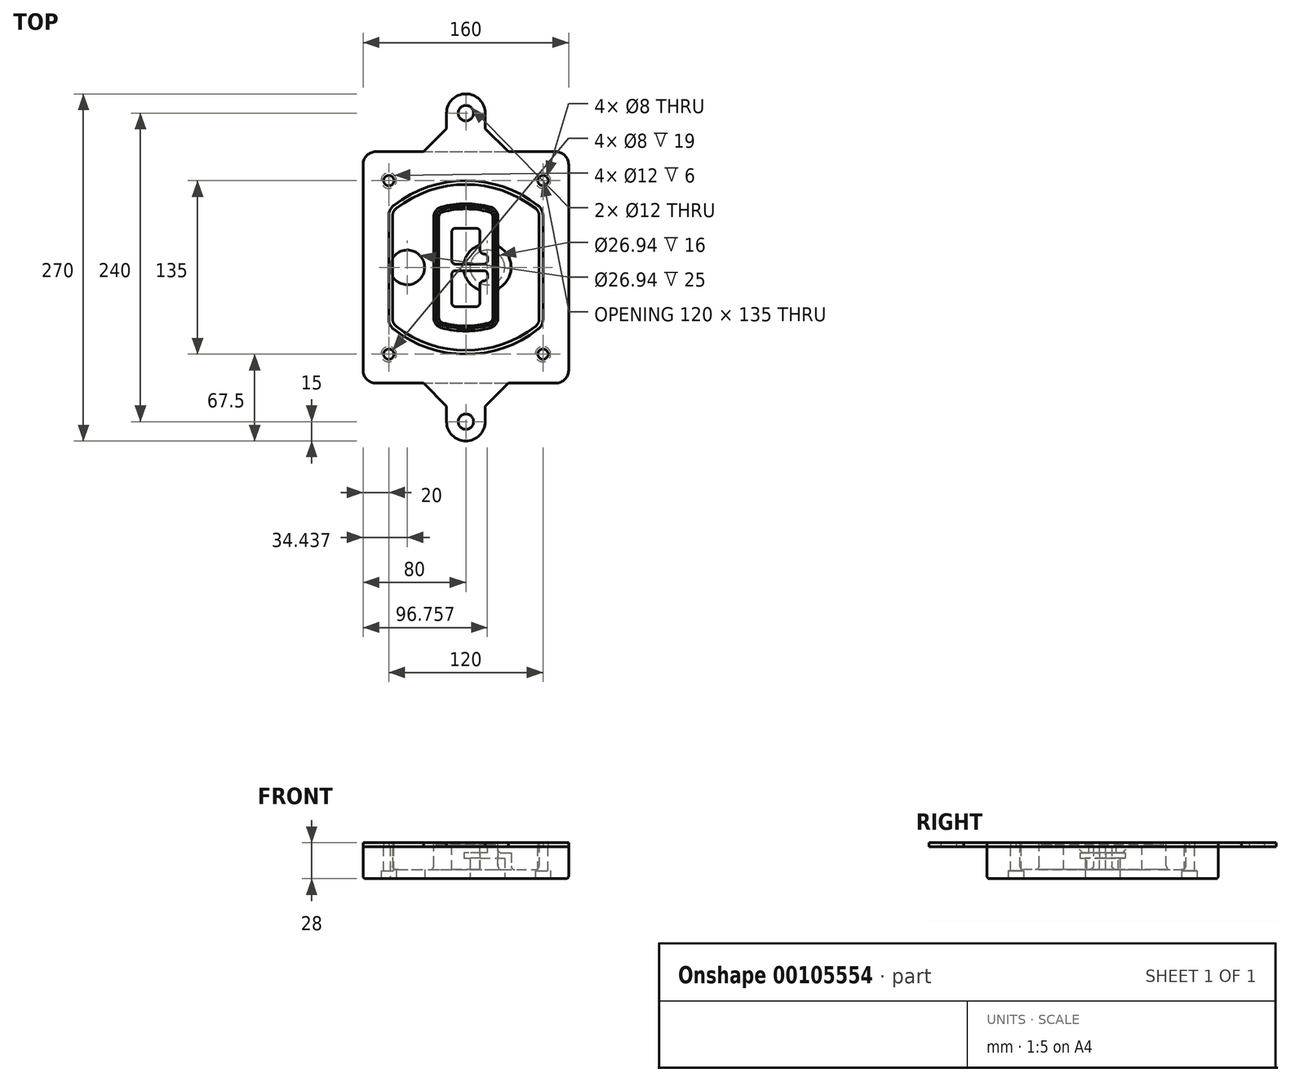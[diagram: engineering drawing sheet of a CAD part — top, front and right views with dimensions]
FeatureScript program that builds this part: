
annotation { "Feature Type Name" : "Feature", "Feature Type Description" : "" }
export const myFeature = defineFeature(function(context is Context, id is Id, definition is map)
    precondition{}
    {
        {
            var Q0;
            Q0=qCreatedBy(makeId("Top.planeOp"),FACE);
            var sketch = newSketch(context, id + "F0", { "sketchPlane" : qUnion([Q0])});
            skPoint(sketch, "E0.rect.middle", {"position": v(0, 0) * mm});
            skLineSegment(sketch, "E1.bottom", {"start": v(-70, -90) * mm, "end": v(70, -90) * mm});
            skLineSegment(sketch, "E1.top", {"start": v(-70, 90) * mm, "end": v(70, 90) * mm});
            skLineSegment(sketch, "E1.left", {"start": v(-80, -80) * mm, "end": v(-80, 80) * mm});
            skLineSegment(sketch, "E1.right", {"start": v(80, -80) * mm, "end": v(80, 80) * mm});
            skLineSegment(sketch, "E2", {"start": v(-80, 90) * mm, "end": v(80, -90) * mm, "construction": true});
            skLineSegment(sketch, "E3", {"start": v(80, 90) * mm, "end": v(-80, -90) * mm, "construction": true});
            skCircle(sketch, "E4", {"center": v(-60, 67.5) * mm, "radius": 4 * mm});
            skCircle(sketch, "E5", {"center": v(60, 67.5) * mm, "radius": 4 * mm});
            skCircle(sketch, "E6", {"center": v(60, -67.5) * mm, "radius": 4 * mm});
            skCircle(sketch, "E7", {"center": v(-60, -67.5) * mm, "radius": 4 * mm});
            skLineSegment(sketch, "E8", {"start": v(-60, 67.5) * mm, "end": v(60, 67.5) * mm, "construction": true});
            skLineSegment(sketch, "E9", {"start": v(60, 67.5) * mm, "end": v(60, -67.5) * mm, "construction": true});
            skLineSegment(sketch, "E10", {"start": v(60, -67.5) * mm, "end": v(-60, -67.5) * mm, "construction": true});
            skLineSegment(sketch, "E11", {"start": v(-60, -67.5) * mm, "end": v(-60, 67.5) * mm, "construction": true});
            skLineSegment(sketch, "E12", {"start": v(-60, 40.3) * mm, "end": v(-60, -40.3) * mm});
            skLineSegment(sketch, "E13", {"start": v(60, 40.3) * mm, "end": v(60, -40.3) * mm});
            skArc(sketch, "E14", {"start": v(56.15, 48.18) * mm, "mid": v(0, 67.5) * mm, "end": v(-56.15, 48.18) * mm});
            skArc(sketch, "E15", {"start": v(-56.15, -48.18) * mm, "mid": v(0, -67.5) * mm, "end": v(56.15, -48.18) * mm});
            skLineSegment(sketch, "E16", {"start": v(-60, 0) * mm, "end": v(60, 0) * mm, "construction": true});
            skPoint(sketch, "E17.visualSharp", {"position": v(-60, -45) * mm});
            skArc(sketch, "E17.filletArc", {"start": v(-60, -40.3) * mm, "mid": v(-58.99, -44.68) * mm, "end": v(-56.15, -48.18) * mm});
            skPoint(sketch, "E18.visualSharp", {"position": v(-60, 45) * mm});
            skArc(sketch, "E18.filletArc", {"start": v(-56.15, 48.18) * mm, "mid": v(-58.99, 44.68) * mm, "end": v(-60, 40.3) * mm});
            skPoint(sketch, "E19.visualSharp", {"position": v(60, 45) * mm});
            skArc(sketch, "E19.filletArc", {"start": v(60, 40.3) * mm, "mid": v(58.99, 44.68) * mm, "end": v(56.15, 48.18) * mm});
            skPoint(sketch, "E20.visualSharp", {"position": v(60, -45) * mm});
            skArc(sketch, "E20.filletArc", {"start": v(56.15, -48.18) * mm, "mid": v(58.99, -44.68) * mm, "end": v(60, -40.3) * mm});
            skPoint(sketch, "E21.visualSharp", {"position": v(-80, 90) * mm});
            skArc(sketch, "E21.filletArc", {"start": v(-70, 90) * mm, "mid": v(-77.07, 87.07) * mm, "end": v(-80, 80) * mm});
            skPoint(sketch, "E22.visualSharp", {"position": v(80, 90) * mm});
            skArc(sketch, "E22.filletArc", {"start": v(80, 80) * mm, "mid": v(77.07, 87.07) * mm, "end": v(70, 90) * mm});
            skPoint(sketch, "E23.visualSharp", {"position": v(80, -90) * mm});
            skArc(sketch, "E23.filletArc", {"start": v(70, -90) * mm, "mid": v(77.07, -87.07) * mm, "end": v(80, -80) * mm});
            skPoint(sketch, "E24.visualSharp", {"position": v(-80, -90) * mm});
            skArc(sketch, "E24.filletArc", {"start": v(-80, -80) * mm, "mid": v(-77.07, -87.07) * mm, "end": v(-70, -90) * mm});
            skArc(sketch, "E25.0", {"start": v(57, 40.3) * mm, "mid": v(56.3, 43.36) * mm, "end": v(54.3, 45.81) * mm});
            skLineSegment(sketch, "E25.1", {"start": v(57, 40.3) * mm, "end": v(57, -40.3) * mm});
            skArc(sketch, "E25.2", {"start": v(54.3, -45.81) * mm, "mid": v(56.3, -43.36) * mm, "end": v(57, -40.3) * mm});
            skArc(sketch, "E25.3", {"start": v(-54.3, -45.81) * mm, "mid": v(0, -64.5) * mm, "end": v(54.3, -45.81) * mm});
            skArc(sketch, "E25.4", {"start": v(-57, -40.3) * mm, "mid": v(-56.3, -43.36) * mm, "end": v(-54.3, -45.81) * mm});
            skArc(sketch, "E25.5", {"start": v(54.3, 45.81) * mm, "mid": v(0, 64.5) * mm, "end": v(-54.3, 45.81) * mm});
            skLineSegment(sketch, "E25.6", {"start": v(-57, 40.3) * mm, "end": v(-57, -40.3) * mm});
            skArc(sketch, "E25.7", {"start": v(-54.3, 45.81) * mm, "mid": v(-56.3, 43.36) * mm, "end": v(-57, 40.3) * mm});
            skArc(sketch, "E26.0", {"start": v(-58.62, 51.33) * mm, "mid": v(-62.58, 46.43) * mm, "end": v(-64, 40.3) * mm});
            skArc(sketch, "E26.1", {"start": v(58.62, 51.33) * mm, "mid": v(0, 71.5) * mm, "end": v(-58.62, 51.33) * mm});
            skArc(sketch, "E26.2", {"start": v(64, 40.3) * mm, "mid": v(62.58, 46.43) * mm, "end": v(58.62, 51.33) * mm});
            skLineSegment(sketch, "E26.3", {"start": v(64, 40.3) * mm, "end": v(64, -40.3) * mm});
            skArc(sketch, "E26.4", {"start": v(58.62, -51.33) * mm, "mid": v(62.58, -46.43) * mm, "end": v(64, -40.3) * mm});
            skLineSegment(sketch, "E26.5", {"start": v(-64, 40.3) * mm, "end": v(-64, -40.3) * mm});
            skArc(sketch, "E26.6", {"start": v(-58.62, -51.33) * mm, "mid": v(0, -71.5) * mm, "end": v(58.62, -51.33) * mm});
            skArc(sketch, "E26.7", {"start": v(-64, -40.3) * mm, "mid": v(-62.58, -46.43) * mm, "end": v(-58.62, -51.33) * mm});
            skSolve(sketch);
        }
        {
            var Q0;
            Q0=makeQuery(id+"F0.imprint","IMPRINT",FACE,{"disambiguationData":[TD([[makeQuery(id+"F0.imprint","IMPRINT",EDGE,{"derivedFrom":sQuery(id+"F0.wireOp",EDGE,"E1.bottom")}),1.0]])]});
            var Q1;
            Q1=makeQuery(id+"F0.imprint","IMPRINT",FACE,{"disambiguationData":[TD([[makeQuery(id+"F0.imprint","IMPRINT",EDGE,{"derivedFrom":sQuery(id+"F0.wireOp",EDGE,"E12")}),1.0]])]});
            var Q2;
            Q2=makeQuery(id+"F0.imprint","IMPRINT",FACE,{"disambiguationData":[TD([[makeQuery(id+"F0.imprint","IMPRINT",EDGE,{"derivedFrom":sQuery(id+"F0.wireOp",EDGE,"E25.0")}),1.0]])]});
            var Q3;
            Q3=makeQuery(id+"F0.imprint","IMPRINT",FACE,{"disambiguationData":[TD([[makeQuery(id+"F0.imprint","IMPRINT",EDGE,{"derivedFrom":sQuery(id+"F0.wireOp",EDGE,"E12")}),-1.0]])]});
            extrude(context, id + "F1", {"entities" : qUnion([Q0, Q1, Q2, Q3]), "oppositeDirection" : true, "depth" : 25 * mm});
        }
        {
            var Q0;
            Q0=makeQuery(id+"F0.imprint","IMPRINT",FACE,{"disambiguationData":[TD([[makeQuery(id+"F0.imprint","IMPRINT",EDGE,{"derivedFrom":sQuery(id+"F0.wireOp",EDGE,"E12")}),1.0]])]});
            extrude(context, id + "F2", {"entities" : qUnion([Q0]), "operationType" : NewBodyOperationType.ADD, "depth" : 3 * mm});
        }
        {
            var Q0;
            Q0=makeQuery(id+"F0.imprint","IMPRINT",FACE,{"disambiguationData":[TD([[makeQuery(id+"F0.imprint","IMPRINT",EDGE,{"derivedFrom":sQuery(id+"F0.wireOp",EDGE,"E25.0")}),1.0]])]});
            extrude(context, id + "F3", {"entities" : qUnion([Q0]), "operationType" : NewBodyOperationType.REMOVE, "oppositeDirection" : true, "depth" : 18 * mm});
        }
        {
            var Q0;
            Q0=makeQuery(id+"F2.opExtrude","CAP_FACE",FACE,{"disambiguationData":[OSD([sQuery(id+"F0.wireOp",EDGE,"E12"),sQuery(id+"F0.wireOp",EDGE,"E13"),sQuery(id+"F0.wireOp",EDGE,"E14"),sQuery(id+"F0.wireOp",EDGE,"E15"),sQuery(id+"F0.wireOp",EDGE,"E17.filletArc"),sQuery(id+"F0.wireOp",EDGE,"E18.filletArc"),sQuery(id+"F0.wireOp",EDGE,"E19.filletArc"),sQuery(id+"F0.wireOp",EDGE,"E20.filletArc"),sQuery(id+"F0.wireOp",EDGE,"E25.0"),sQuery(id+"F0.wireOp",EDGE,"E25.1"),sQuery(id+"F0.wireOp",EDGE,"E25.2"),sQuery(id+"F0.wireOp",EDGE,"E25.3"),sQuery(id+"F0.wireOp",EDGE,"E25.4"),sQuery(id+"F0.wireOp",EDGE,"E25.5"),sQuery(id+"F0.wireOp",EDGE,"E25.6"),sQuery(id+"F0.wireOp",EDGE,"E25.7")])],"isStart":false});
            var sketch = newSketch(context, id + "F4", { "sketchPlane" : qUnion([Q0])});
            skArc(sketch, "E27.0", {"start": v(-19.08, -46.97) * mm, "mid": v(0, -49.5) * mm, "end": v(19.08, -46.97) * mm});
            skArc(sketch, "E28.0", {"start": v(19.08, 46.97) * mm, "mid": v(0, 49.5) * mm, "end": v(-19.08, 46.97) * mm});
            skLineSegment(sketch, "E29", {"start": v(-25, 39.25) * mm, "end": v(-25, -39.25) * mm});
            skLineSegment(sketch, "E30", {"start": v(25, 39.25) * mm, "end": v(25, -39.25) * mm});
            skLineSegment(sketch, "E31", {"start": v(-25, 45.1) * mm, "end": v(25, 45.1) * mm, "construction": true});
            skLineSegment(sketch, "E32", {"start": v(-25, -45.1) * mm, "end": v(25, -45.1) * mm, "construction": true});
            skPoint(sketch, "E33.visualSharp", {"position": v(-25, 45.1) * mm});
            skArc(sketch, "E33.filletArc", {"start": v(-19.08, 46.97) * mm, "mid": v(-23.35, 44.11) * mm, "end": v(-25, 39.25) * mm});
            skPoint(sketch, "E34.visualSharp", {"position": v(25, 45.1) * mm});
            skArc(sketch, "E34.filletArc", {"start": v(25, 39.25) * mm, "mid": v(23.35, 44.11) * mm, "end": v(19.08, 46.97) * mm});
            skPoint(sketch, "E35.visualSharp", {"position": v(25, -45.1) * mm});
            skArc(sketch, "E35.filletArc", {"start": v(19.08, -46.97) * mm, "mid": v(23.35, -44.11) * mm, "end": v(25, -39.25) * mm});
            skPoint(sketch, "E36.visualSharp", {"position": v(-25, -45.1) * mm});
            skArc(sketch, "E36.filletArc", {"start": v(-25, -39.25) * mm, "mid": v(-23.35, -44.11) * mm, "end": v(-19.08, -46.97) * mm});
            skArc(sketch, "E37.0", {"start": v(54.3, 45.81) * mm, "mid": v(0, 64.5) * mm, "end": v(-54.3, 45.81) * mm});
            skArc(sketch, "E37.1", {"start": v(-54.3, 45.81) * mm, "mid": v(-56.3, 43.36) * mm, "end": v(-57, 40.3) * mm});
            skLineSegment(sketch, "E37.2", {"start": v(-57, 40.3) * mm, "end": v(-57, -40.3) * mm});
            skArc(sketch, "E37.3", {"start": v(-57, -40.3) * mm, "mid": v(-56.3, -43.36) * mm, "end": v(-54.3, -45.81) * mm});
            skArc(sketch, "E37.4", {"start": v(-54.3, -45.81) * mm, "mid": v(0, -64.5) * mm, "end": v(54.3, -45.81) * mm});
            skArc(sketch, "E37.5", {"start": v(54.3, -45.81) * mm, "mid": v(56.3, -43.36) * mm, "end": v(57, -40.3) * mm});
            skLineSegment(sketch, "E37.6", {"start": v(57, 40.3) * mm, "end": v(57, -40.3) * mm});
            skArc(sketch, "E37.7", {"start": v(57, 40.3) * mm, "mid": v(56.3, 43.36) * mm, "end": v(54.3, 45.81) * mm});
            skLineSegment(sketch, "E38.0", {"start": v(23, 39.25) * mm, "end": v(23, -39.25) * mm});
            skArc(sketch, "E38.1", {"start": v(18.56, -45.04) * mm, "mid": v(21.76, -42.9) * mm, "end": v(23, -39.25) * mm});
            skArc(sketch, "E38.2", {"start": v(-18.56, -45.04) * mm, "mid": v(0, -47.5) * mm, "end": v(18.56, -45.04) * mm});
            skArc(sketch, "E38.3", {"start": v(-23, -39.25) * mm, "mid": v(-21.76, -42.9) * mm, "end": v(-18.56, -45.04) * mm});
            skLineSegment(sketch, "E38.4", {"start": v(-23, 39.25) * mm, "end": v(-23, -39.25) * mm});
            skArc(sketch, "E38.5", {"start": v(23, 39.25) * mm, "mid": v(21.76, 42.9) * mm, "end": v(18.56, 45.04) * mm});
            skArc(sketch, "E38.6", {"start": v(-18.56, 45.04) * mm, "mid": v(-21.76, 42.9) * mm, "end": v(-23, 39.25) * mm});
            skArc(sketch, "E38.7", {"start": v(18.56, 45.04) * mm, "mid": v(0, 47.5) * mm, "end": v(-18.56, 45.04) * mm});
            skArc(sketch, "E39.0", {"start": v(21, 39.25) * mm, "mid": v(20.18, 41.68) * mm, "end": v(18.04, 43.1) * mm});
            skLineSegment(sketch, "E39.1", {"start": v(21, 39.25) * mm, "end": v(21, -39.25) * mm});
            skArc(sketch, "E39.2", {"start": v(18.04, -43.1) * mm, "mid": v(20.18, -41.68) * mm, "end": v(21, -39.25) * mm});
            skArc(sketch, "E39.3", {"start": v(-18.04, -43.1) * mm, "mid": v(0, -45.5) * mm, "end": v(18.04, -43.1) * mm});
            skArc(sketch, "E39.4", {"start": v(-21, -39.25) * mm, "mid": v(-20.18, -41.68) * mm, "end": v(-18.04, -43.1) * mm});
            skArc(sketch, "E39.5", {"start": v(18.04, 43.1) * mm, "mid": v(0, 45.5) * mm, "end": v(-18.04, 43.1) * mm});
            skLineSegment(sketch, "E39.6", {"start": v(-21, 39.25) * mm, "end": v(-21, -39.25) * mm});
            skArc(sketch, "E39.7", {"start": v(-18.04, 43.1) * mm, "mid": v(-20.18, 41.68) * mm, "end": v(-21, 39.25) * mm});
            skLineSegment(sketch, "E40", {"start": v(-25, 0) * mm, "end": v(25, 0) * mm, "construction": true});
            skLineSegment(sketch, "E41", {"start": v(-11, 5.5) * mm, "end": v(-11, 27.5) * mm});
            skLineSegment(sketch, "E42", {"start": v(-8, 30.5) * mm, "end": v(8, 30.5) * mm});
            skLineSegment(sketch, "E43", {"start": v(11, 27.5) * mm, "end": v(11, 13.5) * mm});
            skLineSegment(sketch, "E44", {"start": v(14, 10.5) * mm, "end": v(14, 10.5) * mm});
            skLineSegment(sketch, "E45", {"start": v(17, 7.5) * mm, "end": v(17, 5.5) * mm});
            skLineSegment(sketch, "E46", {"start": v(14, 2.5) * mm, "end": v(-8, 2.5) * mm});
            skPoint(sketch, "E47.visualSharp", {"position": v(-11, 30.5) * mm});
            skArc(sketch, "E47.filletArc", {"start": v(-8, 30.5) * mm, "mid": v(-10.12, 29.62) * mm, "end": v(-11, 27.5) * mm});
            skPoint(sketch, "E48.visualSharp", {"position": v(11, 30.5) * mm});
            skArc(sketch, "E48.filletArc", {"start": v(11, 27.5) * mm, "mid": v(10.12, 29.62) * mm, "end": v(8, 30.5) * mm});
            skPoint(sketch, "E49.visualSharp", {"position": v(11, 10.5) * mm});
            skArc(sketch, "E49.filletArc", {"start": v(11, 13.5) * mm, "mid": v(11.88, 11.38) * mm, "end": v(14, 10.5) * mm});
            skPoint(sketch, "E50.visualSharp", {"position": v(17, 10.5) * mm});
            skArc(sketch, "E50.filletArc", {"start": v(17, 7.5) * mm, "mid": v(16.12, 9.62) * mm, "end": v(14, 10.5) * mm});
            skPoint(sketch, "E51.visualSharp", {"position": v(17, 2.5) * mm});
            skArc(sketch, "E51.filletArc", {"start": v(14, 2.5) * mm, "mid": v(16.12, 3.38) * mm, "end": v(17, 5.5) * mm});
            skPoint(sketch, "E52.visualSharp", {"position": v(-11, 2.5) * mm});
            skArc(sketch, "E52.filletArc", {"start": v(-11, 5.5) * mm, "mid": v(-10.12, 3.38) * mm, "end": v(-8, 2.5) * mm});
            skLineSegment(sketch, "E53.0.MirrorCS", {"start": v(14, -2.5) * mm, "end": v(-8, -2.5) * mm});
            skArc(sketch, "E54.0.MirrorCS", {"start": v(-11, -5.5) * mm, "mid": v(-10.12, -3.38) * mm, "end": v(-8, -2.5) * mm});
            skLineSegment(sketch, "E55.0.MirrorCS", {"start": v(-11, -5.5) * mm, "end": v(-11, -27.5) * mm});
            skArc(sketch, "E56.0.MirrorCS", {"start": v(-8, -30.5) * mm, "mid": v(-10.12, -29.62) * mm, "end": v(-11, -27.5) * mm});
            skLineSegment(sketch, "E57.0.MirrorCS", {"start": v(-8, -30.5) * mm, "end": v(8, -30.5) * mm});
            skArc(sketch, "E58.0.MirrorCS", {"start": v(11, -27.5) * mm, "mid": v(10.12, -29.62) * mm, "end": v(8, -30.5) * mm});
            skLineSegment(sketch, "E59.0.MirrorCS", {"start": v(11, -27.5) * mm, "end": v(11, -13.5) * mm});
            skArc(sketch, "E60.0.MirrorCS", {"start": v(11, -13.5) * mm, "mid": v(11.88, -11.38) * mm, "end": v(14, -10.5) * mm});
            skArc(sketch, "E61.0.MirrorCS", {"start": v(17, -7.5) * mm, "mid": v(16.12, -9.62) * mm, "end": v(14, -10.5) * mm});
            skLineSegment(sketch, "E62.0.MirrorCS", {"start": v(17, -7.5) * mm, "end": v(17, -5.5) * mm});
            skArc(sketch, "E63.0.MirrorCS", {"start": v(14, -2.5) * mm, "mid": v(16.12, -3.38) * mm, "end": v(17, -5.5) * mm});
            skSolve(sketch);
        }
        {
            var Q0;
            Q0=makeQuery(id+"F4.imprint","IMPRINT",FACE,{"disambiguationData":[TD([[makeQuery(id+"F4.imprint","IMPRINT",EDGE,{"derivedFrom":sQuery(id+"F4.wireOp",EDGE,"E27.0")}),1.0]])]});
            var Q1;
            Q1=makeQuery(id+"F4.imprint","IMPRINT",FACE,{"disambiguationData":[TD([[makeQuery(id+"F4.imprint","IMPRINT",EDGE,{"derivedFrom":sQuery(id+"F4.wireOp",EDGE,"E38.0")}),-1.0]])]});
            var Q2;
            Q2=makeQuery(id+"F4.imprint","IMPRINT",FACE,{"disambiguationData":[TD([[makeQuery(id+"F4.imprint","IMPRINT",EDGE,{"derivedFrom":sQuery(id+"F4.wireOp",EDGE,"E39.0")}),1.0]])]});
            extrude(context, id + "F5", {"entities" : qUnion([Q0, Q1, Q2]), "operationType" : NewBodyOperationType.ADD, "endBound" : BoundingType.UP_TO_NEXT, "oppositeDirection" : true, "depth" : 25 * mm});
        }
        {
            var Q0;
            Q0=makeQuery(id+"F4.imprint","IMPRINT",FACE,{"disambiguationData":[TD([[makeQuery(id+"F4.imprint","IMPRINT",EDGE,{"derivedFrom":sQuery(id+"F4.wireOp",EDGE,"E38.0")}),-1.0]])]});
            extrude(context, id + "F6", {"entities" : qUnion([Q0]), "operationType" : NewBodyOperationType.REMOVE, "oppositeDirection" : true, "depth" : 2 * mm});
        }
        {
            var Q0;
            Q0=makeQuery(id+"F1.opExtrude","CAP_FACE",FACE,{"disambiguationData":[OSD([sQuery(id+"F0.wireOp",EDGE,"E1.bottom"),sQuery(id+"F0.wireOp",EDGE,"E1.top"),sQuery(id+"F0.wireOp",EDGE,"E1.left"),sQuery(id+"F0.wireOp",EDGE,"E1.right"),sQuery(id+"F0.wireOp",EDGE,"E4"),sQuery(id+"F0.wireOp",EDGE,"E5"),sQuery(id+"F0.wireOp",EDGE,"E6"),sQuery(id+"F0.wireOp",EDGE,"E7"),sQuery(id+"F0.wireOp",EDGE,"E21.filletArc"),sQuery(id+"F0.wireOp",EDGE,"E22.filletArc"),sQuery(id+"F0.wireOp",EDGE,"E23.filletArc"),sQuery(id+"F0.wireOp",EDGE,"E24.filletArc")])],"isStart":false});
            var sketch = newSketch(context, id + "F7", { "sketchPlane" : qUnion([Q0])});
            skCircle(sketch, "E64", {"center": v(16.76, 0) * mm, "radius": 13.47 * mm});
            skCircle(sketch, "E65", {"center": v(-45.56, 0) * mm, "radius": 13.47 * mm});
            skLineSegment(sketch, "E66", {"start": v(80, 0) * mm, "end": v(-80, 0) * mm});
            skCircle(sketch, "E67", {"center": v(16.76, 0) * mm, "radius": 18.47 * mm});
            skCircle(sketch, "E68", {"center": v(60, -67.5) * mm, "radius": 6 * mm});
            skCircle(sketch, "E69", {"center": v(-60, -67.5) * mm, "radius": 6 * mm});
            skCircle(sketch, "E70", {"center": v(-60, 67.5) * mm, "radius": 6 * mm});
            skCircle(sketch, "E71", {"center": v(60, 67.5) * mm, "radius": 6 * mm});
            skSolve(sketch);
        }
        {
            var Q0;
            {var subQ1=sQuery(id+"F7.wireOp",EDGE,"E66");var subQ4=sQuery(id+"F7.wireOp",EDGE,"E64");var subQ6=makeQuery(id+"F7.imprint","INTERSECT",VERTEX,{"disambiguationData":[OD(0.0)],"derivedFrom":[subQ4,subQ1]});Q0=makeQuery(id+"F7.imprint","IMPRINT",FACE,{"disambiguationData":[TD([[makeQuery(id+"F7.imprint","IMPRINT",EDGE,{"disambiguationData":[TD([[subQ6,-1.0]])],"derivedFrom":subQ4}),-1.0]])]});}
            var Q1;
            {var subQ0=sQuery(id+"F7.wireOp",EDGE,"E66");var subQ1=sQuery(id+"F7.wireOp",EDGE,"E64");var subQ3=makeQuery(id+"F7.imprint","INTERSECT",VERTEX,{"disambiguationData":[OD(0.0)],"derivedFrom":[subQ1,subQ0]});Q1=makeQuery(id+"F7.imprint","IMPRINT",FACE,{"disambiguationData":[TD([[makeQuery(id+"F7.imprint","IMPRINT",EDGE,{"disambiguationData":[TD([[subQ3,-1.0]])],"derivedFrom":subQ1}),1.0]])]});}
            var Q2;
            {var subQ0=sQuery(id+"F7.wireOp",EDGE,"E66");var subQ1=sQuery(id+"F7.wireOp",EDGE,"E64");var subQ3=makeQuery(id+"F7.imprint","INTERSECT",VERTEX,{"disambiguationData":[OD(0.0)],"derivedFrom":[subQ1,subQ0]});Q2=makeQuery(id+"F7.imprint","IMPRINT",FACE,{"disambiguationData":[TD([[makeQuery(id+"F7.imprint","IMPRINT",EDGE,{"disambiguationData":[TD([[subQ3,1.0]])],"derivedFrom":subQ1}),1.0]])]});}
            var Q3;
            {var subQ1=sQuery(id+"F7.wireOp",EDGE,"E66");var subQ4=sQuery(id+"F7.wireOp",EDGE,"E64");var subQ6=makeQuery(id+"F7.imprint","INTERSECT",VERTEX,{"disambiguationData":[OD(0.0)],"derivedFrom":[subQ4,subQ1]});Q3=makeQuery(id+"F7.imprint","IMPRINT",FACE,{"disambiguationData":[TD([[makeQuery(id+"F7.imprint","IMPRINT",EDGE,{"disambiguationData":[TD([[subQ6,1.0]])],"derivedFrom":subQ4}),-1.0]])]});}
            extrude(context, id + "F8", {"entities" : qUnion([Q0, Q1, Q2, Q3]), "operationType" : NewBodyOperationType.ADD, "oppositeDirection" : true, "depth" : 20 * mm});
        }
        {
            var Q0;
            {var subQ0=sQuery(id+"F7.wireOp",EDGE,"E66");var subQ1=sQuery(id+"F7.wireOp",EDGE,"E64");var subQ3=makeQuery(id+"F7.imprint","INTERSECT",VERTEX,{"disambiguationData":[OD(0.0)],"derivedFrom":[subQ1,subQ0]});Q0=makeQuery(id+"F7.imprint","IMPRINT",FACE,{"disambiguationData":[TD([[makeQuery(id+"F7.imprint","IMPRINT",EDGE,{"disambiguationData":[TD([[subQ3,-1.0]])],"derivedFrom":subQ1}),1.0]])]});}
            var Q1;
            {var subQ0=sQuery(id+"F7.wireOp",EDGE,"E66");var subQ1=sQuery(id+"F7.wireOp",EDGE,"E64");var subQ3=makeQuery(id+"F7.imprint","INTERSECT",VERTEX,{"disambiguationData":[OD(0.0)],"derivedFrom":[subQ1,subQ0]});Q1=makeQuery(id+"F7.imprint","IMPRINT",FACE,{"disambiguationData":[TD([[makeQuery(id+"F7.imprint","IMPRINT",EDGE,{"disambiguationData":[TD([[subQ3,1.0]])],"derivedFrom":subQ1}),1.0]])]});}
            extrude(context, id + "F9", {"entities" : qUnion([Q0, Q1]), "operationType" : NewBodyOperationType.REMOVE, "oppositeDirection" : true, "depth" : 16 * mm});
        }
        {
            var Q0;
            {var subQ0=sQuery(id+"F7.wireOp",EDGE,"E66");var subQ1=sQuery(id+"F7.wireOp",EDGE,"E65");var subQ3=makeQuery(id+"F7.imprint","INTERSECT",VERTEX,{"disambiguationData":[OD(0.0)],"derivedFrom":[subQ1,subQ0]});Q0=makeQuery(id+"F7.imprint","IMPRINT",FACE,{"disambiguationData":[TD([[makeQuery(id+"F7.imprint","IMPRINT",EDGE,{"disambiguationData":[TD([[subQ3,-1.0]])],"derivedFrom":subQ1}),1.0]])]});}
            var Q1;
            {var subQ0=sQuery(id+"F7.wireOp",EDGE,"E66");var subQ1=sQuery(id+"F7.wireOp",EDGE,"E65");var subQ3=makeQuery(id+"F7.imprint","INTERSECT",VERTEX,{"disambiguationData":[OD(0.0)],"derivedFrom":[subQ1,subQ0]});Q1=makeQuery(id+"F7.imprint","IMPRINT",FACE,{"disambiguationData":[TD([[makeQuery(id+"F7.imprint","IMPRINT",EDGE,{"disambiguationData":[TD([[subQ3,1.0]])],"derivedFrom":subQ1}),1.0]])]});}
            extrude(context, id + "F10", {"entities" : qUnion([Q0, Q1]), "operationType" : NewBodyOperationType.REMOVE, "oppositeDirection" : true, "depth" : 25 * mm});
        }
        {
            var Q0;
            Q0=makeQuery(id+"F7.imprint","IMPRINT",FACE,{"disambiguationData":[TD([[makeQuery(id+"F7.imprint","IMPRINT",EDGE,{"derivedFrom":sQuery(id+"F7.wireOp",EDGE,"E68")}),1.0]])]});
            var Q1;
            Q1=makeQuery(id+"F7.imprint","IMPRINT",FACE,{"disambiguationData":[TD([[makeQuery(id+"F7.imprint","IMPRINT",EDGE,{"derivedFrom":makeQuery(id+"F1.opExtrude","CAP_EDGE",EDGE,{"disambiguationData":[OSD([sQuery(id+"F0.wireOp",EDGE,"E5")])],"isStart":false})}),-1.0]])]});
            var Q2;
            Q2=makeQuery(id+"F7.imprint","IMPRINT",FACE,{"disambiguationData":[TD([[makeQuery(id+"F7.imprint","IMPRINT",EDGE,{"derivedFrom":sQuery(id+"F7.wireOp",EDGE,"E69")}),1.0]])]});
            var Q3;
            Q3=makeQuery(id+"F7.imprint","IMPRINT",FACE,{"disambiguationData":[TD([[makeQuery(id+"F7.imprint","IMPRINT",EDGE,{"derivedFrom":makeQuery(id+"F1.opExtrude","CAP_EDGE",EDGE,{"disambiguationData":[OSD([sQuery(id+"F0.wireOp",EDGE,"E4")])],"isStart":false})}),-1.0]])]});
            var Q4;
            Q4=makeQuery(id+"F7.imprint","IMPRINT",FACE,{"disambiguationData":[TD([[makeQuery(id+"F7.imprint","IMPRINT",EDGE,{"derivedFrom":sQuery(id+"F7.wireOp",EDGE,"E70")}),1.0]])]});
            var Q5;
            Q5=makeQuery(id+"F7.imprint","IMPRINT",FACE,{"disambiguationData":[TD([[makeQuery(id+"F7.imprint","IMPRINT",EDGE,{"derivedFrom":makeQuery(id+"F1.opExtrude","CAP_EDGE",EDGE,{"disambiguationData":[OSD([sQuery(id+"F0.wireOp",EDGE,"E7")])],"isStart":false})}),-1.0]])]});
            var Q6;
            Q6=makeQuery(id+"F7.imprint","IMPRINT",FACE,{"disambiguationData":[TD([[makeQuery(id+"F7.imprint","IMPRINT",EDGE,{"derivedFrom":sQuery(id+"F7.wireOp",EDGE,"E71")}),1.0]])]});
            var Q7;
            Q7=makeQuery(id+"F7.imprint","IMPRINT",FACE,{"disambiguationData":[TD([[makeQuery(id+"F7.imprint","IMPRINT",EDGE,{"derivedFrom":makeQuery(id+"F1.opExtrude","CAP_EDGE",EDGE,{"disambiguationData":[OSD([sQuery(id+"F0.wireOp",EDGE,"E6")])],"isStart":false})}),-1.0]])]});
            extrude(context, id + "F11", {"entities" : qUnion([Q0, Q1, Q2, Q3, Q4, Q5, Q6, Q7]), "operationType" : NewBodyOperationType.REMOVE, "oppositeDirection" : true, "depth" : 6 * mm});
        }
        {
            var Q0;
            Q0=makeQuery(id+"F9.boolean.opBoolean","COPY",FACE,{"derivedFrom":makeQuery(id+"F9.opExtrude","CAP_FACE",FACE,{"disambiguationData":[OSD([sQuery(id+"F7.wireOp",EDGE,"E64")])],"isStart":false})});
            var sketch = newSketch(context, id + "F12", { "sketchPlane" : qUnion([Q0])});
            skArc(sketch, "E72.0", {"start": v(11, 17.55) * mm, "mid": v(2.57, 11.82) * mm, "end": v(-1.54, 2.5) * mm});
            skArc(sketch, "E72.1", {"start": v(-1.54, -2.5) * mm, "mid": v(2.57, -11.82) * mm, "end": v(11, -17.55) * mm});
            skLineSegment(sketch, "E73", {"start": v(-1.54, -2.5) * mm, "end": v(14, -2.5) * mm});
            skLineSegment(sketch, "E74.0", {"start": v(14, 2.5) * mm, "end": v(-1.54, 2.5) * mm});
            skArc(sketch, "E74.1", {"start": v(14, 2.5) * mm, "mid": v(16.12, 3.38) * mm, "end": v(17, 5.5) * mm});
            skLineSegment(sketch, "E74.2", {"start": v(17, 7.5) * mm, "end": v(17, 5.5) * mm});
            skArc(sketch, "E74.3", {"start": v(17, 7.5) * mm, "mid": v(16.12, 9.62) * mm, "end": v(14, 10.5) * mm});
            skArc(sketch, "E74.4", {"start": v(11, 13.5) * mm, "mid": v(11.88, 11.38) * mm, "end": v(14, 10.5) * mm});
            skLineSegment(sketch, "E74.5", {"start": v(11, 17.55) * mm, "end": v(11, 13.5) * mm});
            skLineSegment(sketch, "E74.7", {"start": v(14, -2.5) * mm, "end": v(-1.54, -2.5) * mm});
            skArc(sketch, "E74.8", {"start": v(14, -2.5) * mm, "mid": v(16.12, -3.38) * mm, "end": v(17, -5.5) * mm});
            skLineSegment(sketch, "E74.9", {"start": v(17, -7.5) * mm, "end": v(17, -5.5) * mm});
            skArc(sketch, "E74.10", {"start": v(17, -7.5) * mm, "mid": v(16.12, -9.62) * mm, "end": v(14, -10.5) * mm});
            skArc(sketch, "E74.11", {"start": v(11, -13.5) * mm, "mid": v(11.88, -11.38) * mm, "end": v(14, -10.5) * mm});
            skLineSegment(sketch, "E74.12", {"start": v(11, -17.55) * mm, "end": v(11, -13.5) * mm});
            skPoint(sketch, "E75.orphan", {"position": v(11, -27.5) * mm});
            skPoint(sketch, "E76.orphan", {"position": v(-8, -2.5) * mm});
            skPoint(sketch, "E77.orphan", {"position": v(-8, 2.5) * mm});
            skPoint(sketch, "E78.orphan", {"position": v(11, 27.5) * mm});
            skSolve(sketch);
        }
        {
            var Q0;
            {var subQ7=sQuery(id+"F12.wireOp",EDGE,"E72.0");var subQ14=sQuery(id+"F12.wireOp",EDGE,"E72.1");var subQ16=sQuery(id+"F12.wireOp",EDGE,"E74.1");var subQ18=sQuery(id+"F12.wireOp",EDGE,"E74.8");Q0=qUnion([makeQuery(id+"F12.imprint","IMPRINT",FACE,{"disambiguationData":[TD([[makeQuery(id+"F12.imprint","IMPRINT",EDGE,{"derivedFrom":subQ7}),1.0]])]}),makeQuery(id+"F12.imprint","IMPRINT",FACE,{"disambiguationData":[TD([[makeQuery(id+"F12.imprint","IMPRINT",EDGE,{"derivedFrom":subQ14}),1.0]])]}),makeQuery(id+"F12.imprint","IMPRINT",FACE,{"disambiguationData":[TD([[makeQuery(id+"F12.imprint","IMPRINT",EDGE,{"derivedFrom":subQ16}),1.0]])]}),makeQuery(id+"F12.imprint","IMPRINT",FACE,{"disambiguationData":[TD([[makeQuery(id+"F12.imprint","IMPRINT",EDGE,{"derivedFrom":subQ18}),-1.0]])]})]);}
            var Q1;
            Q1=makeQuery(id+"F5.boolean.opBoolean","SPLIT",FACE,{"disambiguationData":[TD([makeQuery(id+"F5.opExtrude","SWEPT_FACE",FACE,{"disambiguationData":[OSD([sQuery(id+"F4.wireOp",EDGE,"E41")])]})])],"derivedFrom":makeQuery(id+"F3.boolean.opBoolean","COPY",FACE,{"derivedFrom":makeQuery(id+"F3.opExtrude","CAP_FACE",FACE,{"disambiguationData":[OSD([sQuery(id+"F0.wireOp",EDGE,"E25.0"),sQuery(id+"F0.wireOp",EDGE,"E25.1"),sQuery(id+"F0.wireOp",EDGE,"E25.2"),sQuery(id+"F0.wireOp",EDGE,"E25.3"),sQuery(id+"F0.wireOp",EDGE,"E25.4"),sQuery(id+"F0.wireOp",EDGE,"E25.5"),sQuery(id+"F0.wireOp",EDGE,"E25.6"),sQuery(id+"F0.wireOp",EDGE,"E25.7")])],"isStart":false})})});
            extrude(context, id + "F13", {"entities" : qUnion([Q0]), "operationType" : NewBodyOperationType.REMOVE, "endBound" : BoundingType.UP_TO_SURFACE, "endBoundEntityFace" : qUnion([Q1]), "depth" : 25 * mm});
        }
        {
            var Q0;
            Q0=makeQuery(id+"F3.boolean.opBoolean","COPY",EDGE,{"derivedFrom":makeQuery(id+"F3.opExtrude","CAP_EDGE",EDGE,{"disambiguationData":[OSD([sQuery(id+"F0.wireOp",EDGE,"E25.6")])],"isStart":false})});
            var Q1;
            Q1=makeQuery(id+"F8.boolean.opBoolean","INTERSECT",EDGE,{"derivedFrom":[makeQuery(id+"F5.opExtrude","SWEPT_FACE",FACE,{"disambiguationData":[OSD([sQuery(id+"F4.wireOp",EDGE,"E30")])]}),makeQuery(id+"F8.opExtrude","CAP_FACE",FACE,{"disambiguationData":[OSD([sQuery(id+"F7.wireOp",EDGE,"E67")])],"isStart":false})]});
            var Q2;
            Q2=makeQuery(id+"F8.boolean.opBoolean","INTERSECT",EDGE,{"disambiguationData":[OD(1.0)],"derivedFrom":[makeQuery(id+"F5.opExtrude","SWEPT_FACE",FACE,{"disambiguationData":[OSD([sQuery(id+"F4.wireOp",EDGE,"E30")])]}),makeQuery(id+"F8.opExtrude","SWEPT_FACE",FACE,{"disambiguationData":[OSD([sQuery(id+"F7.wireOp",EDGE,"E67")])]})]});
            var Q3;
            {var subQ0=sQuery(id+"F4.wireOp",EDGE,"E30");Q3=makeQuery(id+"F8.boolean.opBoolean","SPLIT",EDGE,{"disambiguationData":[TD([makeQuery(id+"F5.opExtrude","SWEPT_FACE",FACE,{"disambiguationData":[OSD([sQuery(id+"F4.wireOp",EDGE,"E35.filletArc")])]})])],"derivedFrom":makeQuery(id+"F5.opExtrude","CAP_EDGE",EDGE,{"disambiguationData":[OSD([subQ0])],"isStart":false})});}
            var Q4;
            {var subQ0=sQuery(id+"F0.wireOp",EDGE,"E25.7");var subQ1=sQuery(id+"F0.wireOp",EDGE,"E25.1");var subQ2=sQuery(id+"F0.wireOp",EDGE,"E25.6");var subQ3=sQuery(id+"F0.wireOp",EDGE,"E25.5");var subQ4=sQuery(id+"F0.wireOp",EDGE,"E25.4");var subQ5=sQuery(id+"F0.wireOp",EDGE,"E25.0");var subQ6=sQuery(id+"F0.wireOp",EDGE,"E25.2");var subQ7=sQuery(id+"F0.wireOp",EDGE,"E25.3");Q4=makeQuery(id+"F8.boolean.opBoolean","INTERSECT",EDGE,{"derivedFrom":[makeQuery(id+"F5.boolean.opBoolean","SPLIT",FACE,{"disambiguationData":[TD([makeQuery(id+"F2.opExtrude","SWEPT_FACE",FACE,{"disambiguationData":[OSD([subQ5])]})])],"derivedFrom":makeQuery(id+"F3.boolean.opBoolean","COPY",FACE,{"derivedFrom":makeQuery(id+"F3.opExtrude","CAP_FACE",FACE,{"disambiguationData":[OSD([subQ5,subQ1,subQ6,subQ7,subQ4,subQ3,subQ2,subQ0])],"isStart":false})})}),makeQuery(id+"F8.opExtrude","SWEPT_FACE",FACE,{"disambiguationData":[OSD([sQuery(id+"F7.wireOp",EDGE,"E67")])]})]});}
            var Q5;
            Q5=makeQuery(id+"F8.boolean.opBoolean","INTERSECT",EDGE,{"disambiguationData":[OD(0.0)],"derivedFrom":[makeQuery(id+"F5.opExtrude","SWEPT_FACE",FACE,{"disambiguationData":[OSD([sQuery(id+"F4.wireOp",EDGE,"E30")])]}),makeQuery(id+"F8.opExtrude","SWEPT_FACE",FACE,{"disambiguationData":[OSD([sQuery(id+"F7.wireOp",EDGE,"E67")])]})]});
            fillet(context, id + "F14", {"entities" : qUnion([Q0, Q1, Q2, Q3, Q4, Q5]), "radius" : 3 * mm, "tangentPropagation" : true, "allowEdgeOverflow" : false});
        }
        {
            var Q0;
            Q0=makeQuery(id+"F1.opExtrude","CAP_EDGE",EDGE,{"disambiguationData":[OSD([sQuery(id+"F0.wireOp",EDGE,"E1.bottom")])],"isStart":false});
            fillet(context, id + "F15", {"entities" : qUnion([Q0]), "radius" : 2 * mm, "tangentPropagation" : true, "allowEdgeOverflow" : false});
        }
        {
            var Q0;
            {var subQ0=sQuery(id+"F0.wireOp",EDGE,"E22.filletArc");var subQ1=sQuery(id+"F0.wireOp",EDGE,"E7");var subQ2=sQuery(id+"F0.wireOp",EDGE,"E6");var subQ3=sQuery(id+"F0.wireOp",EDGE,"E5");var subQ4=sQuery(id+"F0.wireOp",EDGE,"E4");var subQ5=sQuery(id+"F0.wireOp",EDGE,"E1.bottom");var subQ6=sQuery(id+"F0.wireOp",EDGE,"E21.filletArc");var subQ7=sQuery(id+"F0.wireOp",EDGE,"E1.top");var subQ8=sQuery(id+"F0.wireOp",EDGE,"E1.left");var subQ9=sQuery(id+"F0.wireOp",EDGE,"E1.right");var subQ10=sQuery(id+"F0.wireOp",EDGE,"E23.filletArc");var subQ11=sQuery(id+"F0.wireOp",EDGE,"E24.filletArc");Q0=makeQuery(id+"F2.boolean.opBoolean","SPLIT",FACE,{"disambiguationData":[TD([makeQuery(id+"F1.opExtrude","SWEPT_FACE",FACE,{"disambiguationData":[OSD([subQ5])]})])],"derivedFrom":makeQuery(id+"F1.opExtrude","CAP_FACE",FACE,{"disambiguationData":[OSD([subQ5,subQ7,subQ8,subQ9,subQ4,subQ3,subQ2,subQ1,subQ6,subQ0,subQ10,subQ11])],"isStart":true})});}
            var sketch = newSketch(context, id + "F16", { "sketchPlane" : qUnion([Q0])});
            skLineSegment(sketch, "E79.0", {"start": v(-70, 90) * mm, "end": v(70, 90) * mm});
            skArc(sketch, "E79.1", {"start": v(-70, 90) * mm, "mid": v(-77.07, 87.07) * mm, "end": v(-80, 80) * mm});
            skLineSegment(sketch, "E79.2", {"start": v(-80, -80) * mm, "end": v(-80, 80) * mm});
            skArc(sketch, "E79.3", {"start": v(-80, -80) * mm, "mid": v(-77.07, -87.07) * mm, "end": v(-70, -90) * mm});
            skLineSegment(sketch, "E79.4", {"start": v(-70, -90) * mm, "end": v(70, -90) * mm});
            skArc(sketch, "E79.5", {"start": v(70, -90) * mm, "mid": v(77.07, -87.07) * mm, "end": v(80, -80) * mm});
            skLineSegment(sketch, "E79.6", {"start": v(80, -80) * mm, "end": v(80, 80) * mm});
            skArc(sketch, "E79.7", {"start": v(80, 80) * mm, "mid": v(77.07, 87.07) * mm, "end": v(70, 90) * mm});
            skCircle(sketch, "E79.8", {"center": v(60, 67.5) * mm, "radius": 4 * mm});
            skCircle(sketch, "E79.9", {"center": v(-60, 67.5) * mm, "radius": 4 * mm});
            skCircle(sketch, "E79.10", {"center": v(-60, -67.5) * mm, "radius": 4 * mm});
            skCircle(sketch, "E79.11", {"center": v(60, -67.5) * mm, "radius": 4 * mm});
            skArc(sketch, "E79.12", {"start": v(-56.15, -48.18) * mm, "mid": v(0, -67.5) * mm, "end": v(56.15, -48.18) * mm});
            skLineSegment(sketch, "E79.13", {"start": v(60, 40.3) * mm, "end": v(60, -40.3) * mm});
            skArc(sketch, "E79.14", {"start": v(56.15, -48.18) * mm, "mid": v(58.99, -44.68) * mm, "end": v(60, -40.3) * mm});
            skArc(sketch, "E79.15", {"start": v(60, 40.3) * mm, "mid": v(58.99, 44.68) * mm, "end": v(56.15, 48.18) * mm});
            skArc(sketch, "E79.16", {"start": v(56.15, 48.18) * mm, "mid": v(0, 67.5) * mm, "end": v(-56.15, 48.18) * mm});
            skArc(sketch, "E79.17", {"start": v(-56.15, 48.18) * mm, "mid": v(-58.99, 44.68) * mm, "end": v(-60, 40.3) * mm});
            skLineSegment(sketch, "E79.18", {"start": v(-60, 40.3) * mm, "end": v(-60, -40.3) * mm});
            skArc(sketch, "E79.19", {"start": v(-60, -40.3) * mm, "mid": v(-58.99, -44.68) * mm, "end": v(-56.15, -48.18) * mm});
            skCircle(sketch, "E80", {"center": v(0, -120) * mm, "radius": 6 * mm});
            skLineSegment(sketch, "E81", {"start": v(15, -120) * mm, "end": v(15, -108) * mm});
            skLineSegment(sketch, "E82", {"start": v(15, -108) * mm, "end": v(33, -90) * mm});
            skLineSegment(sketch, "E83", {"start": v(33, -90) * mm, "end": v(-33, -90) * mm});
            skLineSegment(sketch, "E84", {"start": v(-33, -90) * mm, "end": v(-15, -108) * mm});
            skLineSegment(sketch, "E85", {"start": v(-15, -108) * mm, "end": v(-15, -120) * mm});
            skArc(sketch, "E86", {"start": v(-15, -120) * mm, "mid": v(0, -135) * mm, "end": v(15, -120) * mm});
            skLineSegment(sketch, "E87", {"start": v(0, -120) * mm, "end": v(0, -90) * mm, "construction": true});
            skLineSegment(sketch, "E88", {"start": v(60, 0) * mm, "end": v(-80, 0) * mm, "construction": true});
            skLineSegment(sketch, "E89.MirrorCS", {"start": v(15, 120) * mm, "end": v(15, 108) * mm});
            skLineSegment(sketch, "E90.MirrorCS", {"start": v(-15, 108) * mm, "end": v(-15, 120) * mm});
            skLineSegment(sketch, "E91.MirrorCS", {"start": v(15, 108) * mm, "end": v(33, 90) * mm});
            skLineSegment(sketch, "E92.MirrorCS", {"start": v(-33, 90) * mm, "end": v(-15, 108) * mm});
            skLineSegment(sketch, "E93.MirrorCS", {"start": v(0, 120) * mm, "end": v(0, 90) * mm, "construction": true});
            skCircle(sketch, "E94.MirrorC", {"center": v(0, 120) * mm, "radius": 6 * mm});
            skArc(sketch, "E95.MirrorCS", {"start": v(-15, 120) * mm, "mid": v(0, 135) * mm, "end": v(15, 120) * mm});
            skSolve(sketch);
        }
        {
            var Q0;
            Q0=makeQuery(id+"F16.imprint","IMPRINT",FACE,{"disambiguationData":[TD([[makeQuery(id+"F16.imprint","IMPRINT",EDGE,{"derivedFrom":sQuery(id+"F16.wireOp",EDGE,"E89.MirrorCS")}),-1.0]])]});
            var Q1;
            Q1=makeQuery(id+"F16.imprint","IMPRINT",FACE,{"disambiguationData":[TD([[makeQuery(id+"F16.imprint","IMPRINT",EDGE,{"derivedFrom":sQuery(id+"F16.wireOp",EDGE,"E80")}),-1.0]])]});
            var Q2;
            {var subQ1=sQuery(id+"F16.wireOp",EDGE,"E79.1");Q2=makeQuery(id+"F16.imprint","IMPRINT",FACE,{"disambiguationData":[TD([[makeQuery(id+"F16.imprint","IMPRINT",EDGE,{"derivedFrom":subQ1}),1.0]])]});}
            var Q3;
            Q3=makeQuery(id+"F2.opExtrude","CAP_FACE",FACE,{"disambiguationData":[OSD([sQuery(id+"F0.wireOp",EDGE,"E12"),sQuery(id+"F0.wireOp",EDGE,"E13"),sQuery(id+"F0.wireOp",EDGE,"E14"),sQuery(id+"F0.wireOp",EDGE,"E15"),sQuery(id+"F0.wireOp",EDGE,"E17.filletArc"),sQuery(id+"F0.wireOp",EDGE,"E18.filletArc"),sQuery(id+"F0.wireOp",EDGE,"E19.filletArc"),sQuery(id+"F0.wireOp",EDGE,"E20.filletArc"),sQuery(id+"F0.wireOp",EDGE,"E25.0"),sQuery(id+"F0.wireOp",EDGE,"E25.1"),sQuery(id+"F0.wireOp",EDGE,"E25.2"),sQuery(id+"F0.wireOp",EDGE,"E25.3"),sQuery(id+"F0.wireOp",EDGE,"E25.4"),sQuery(id+"F0.wireOp",EDGE,"E25.5"),sQuery(id+"F0.wireOp",EDGE,"E25.6"),sQuery(id+"F0.wireOp",EDGE,"E25.7")])],"isStart":false});
            extrude(context, id + "F17", {"entities" : qUnion([Q0, Q1, Q2]), "endBound" : BoundingType.UP_TO_SURFACE, "endBoundEntityFace" : qUnion([Q3]), "depth" : 25 * mm});
        }
    });
